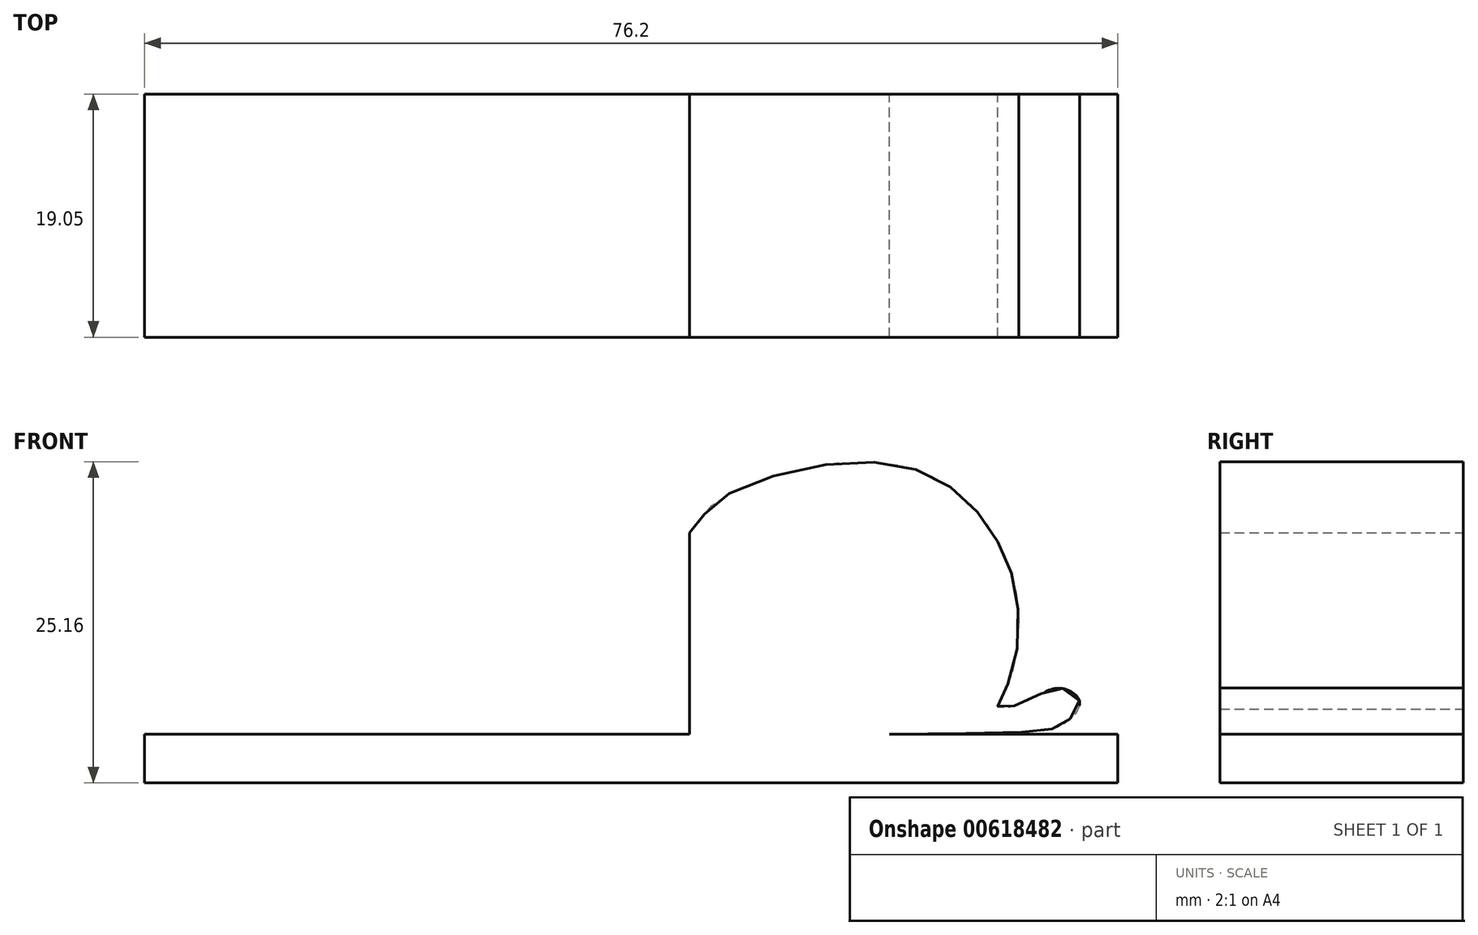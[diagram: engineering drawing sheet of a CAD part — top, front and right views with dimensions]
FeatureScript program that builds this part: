
annotation { "Feature Type Name" : "Feature", "Feature Type Description" : "" }
export const myFeature = defineFeature(function(context is Context, id is Id, definition is map)
    precondition{}
    {
        {
            var Q0;
            Q0=qCreatedBy(makeId("Top.planeOp"),FACE);
            var sketch = newSketch(context, id + "F0", { "sketchPlane" : qUnion([Q0])});
            skLineSegment(sketch, "E0.bottom", {"start": v(-30.63, 16.02) * mm, "end": v(45.57, 16.02) * mm});
            skLineSegment(sketch, "E0.top", {"start": v(-30.63, -3.03) * mm, "end": v(45.57, -3.03) * mm});
            skLineSegment(sketch, "E0.left", {"start": v(-30.63, 16.02) * mm, "end": v(-30.63, -3.03) * mm});
            skLineSegment(sketch, "E0.right", {"start": v(45.57, 16.02) * mm, "end": v(45.57, -3.03) * mm});
            skSolve(sketch);
        }
        {
            var Q0;
            Q0=makeQuery(id+"F0.imprint","IMPRINT",FACE,{"disambiguationData":[TD([[makeQuery(id+"F0.imprint","IMPRINT",EDGE,{"derivedFrom":sQuery(id+"F0.wireOp",EDGE,"E0.bottom")}),-1.0]])]});
            extrude(context, id + "F1", {"entities" : qUnion([Q0]), "depth" : 3.8 * mm, "offsetDistance" : 25.4 * mm});
        }
        {
            var Q0;
            Q0=makeQuery(id+"F1.opExtrude","SWEPT_FACE",FACE,{"disambiguationData":[OSD([sQuery(id+"F0.wireOp",EDGE,"E0.bottom")])]});
            cPlane(context, id + "F2", {"entities" : qUnion([Q0]), "cplaneType" : CPlaneType.OFFSET, "offset" : 0 * mm, "width" : 152.4 * mm, "height" : 152.4 * mm});
        }
        {
            var Q0;
            Q0=qCreatedBy(id+"F2.planeOp",FACE);
            var sketch = newSketch(context, id + "F3", { "sketchPlane" : qUnion([Q0])});
            skCircle(sketch, "E1", {"center": v(-25.25, 12.7) * mm, "radius": 10.16 * mm});
            skCircle(sketch, "E2", {"center": v(10.3, 12.7) * mm, "radius": 10.16 * mm});
            skSolve(sketch);
        }
        {
            var Q0;
            Q0=qCreatedBy(id+"F2.planeOp",FACE);
            var sketch = newSketch(context, id + "F4", { "sketchPlane" : qUnion([Q0])});
            skLineSegment(sketch, "E3", {"start": v(-12.05, 4.35) * mm, "end": v(-12.05, 19.59) * mm});
            skFitSpline(sketch, "E4", {"points": [v(-12.05, 19.59) * mm, v(-13.83, 21.79) * mm, v(-23.3, 25.02) * mm, v(-31.44, 23.82) * mm, v(-35.75, 19.59) * mm, v(-37.67, 14.48) * mm, v(-37.07, 8.01) * mm, v(-36.23, 5.86) * mm, v(-38.75, 6.58) * mm, v(-41.14, 7.41) * mm, v(-42.58, 6.34) * mm, v(-41.38, 4.66) * mm, v(-39.23, 4.06) * mm, v(-12.05, 3.79) * mm], "startDerivative": vector(-41.66, 31.24) * mm, "endDerivative": vector(206.1, 0.09) * mm});
            skLineSegment(sketch, "E5", {"start": v(-12.05, 3.79) * mm, "end": v(-12.05, 4.35) * mm});
            skSolve(sketch);
        }
        {
            var Q0;
            Q0 = qSketchRegion(id + "F4", true);
            extrude(context, id + "F5", {"entities" : qUnion([Q0]), "operationType" : NewBodyOperationType.ADD, "depth" : -19.05 * mm, "offsetDistance" : 25.4 * mm});
        }
    });
